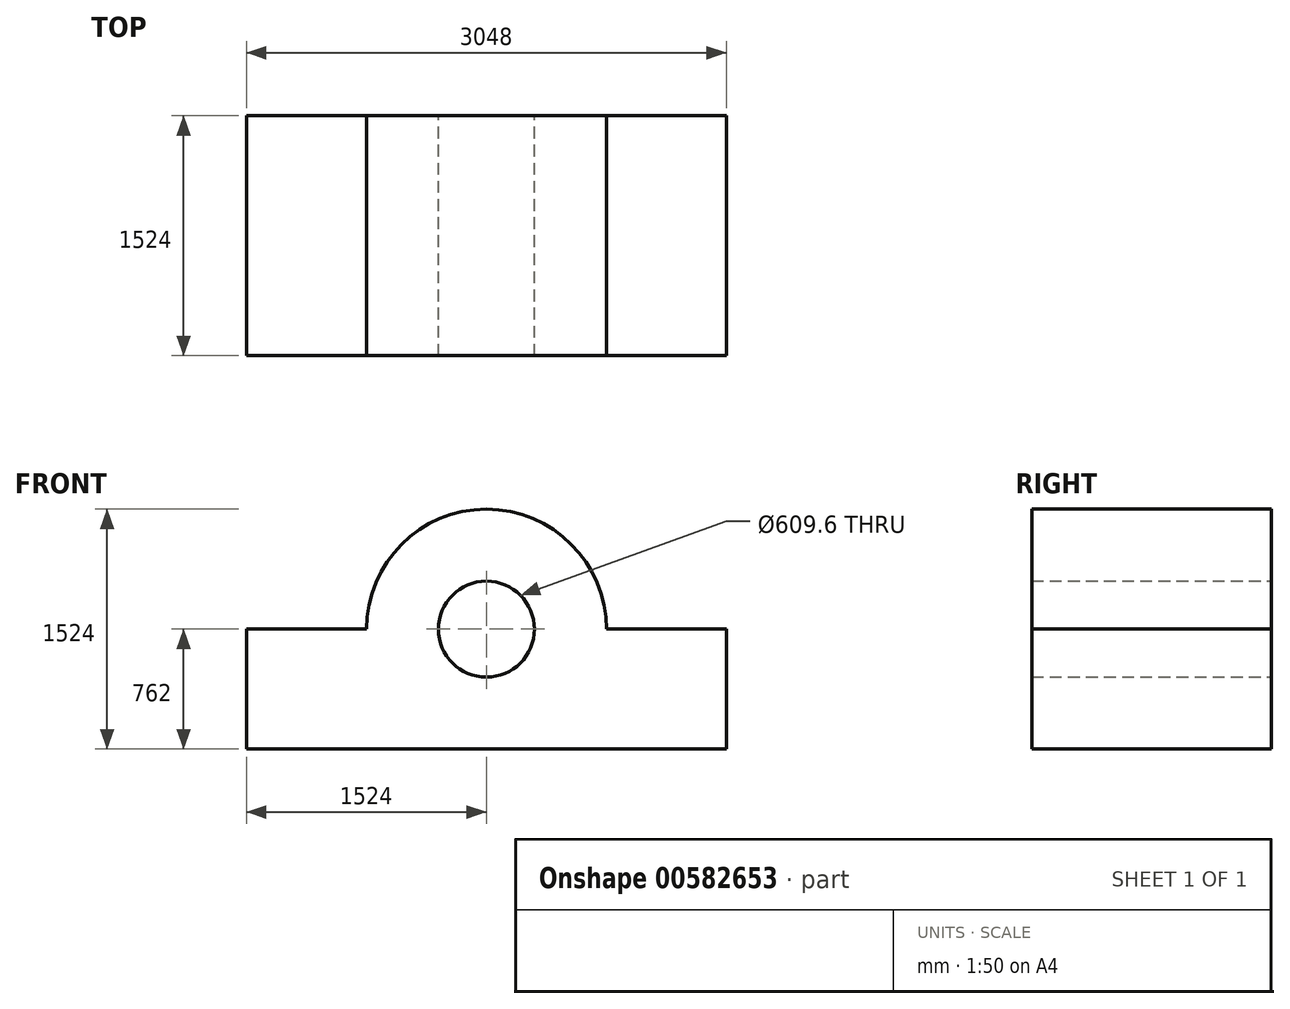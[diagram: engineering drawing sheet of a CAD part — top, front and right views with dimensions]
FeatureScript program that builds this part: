
annotation { "Feature Type Name" : "Feature", "Feature Type Description" : "" }
export const myFeature = defineFeature(function(context is Context, id is Id, definition is map)
    precondition{}
    {
        {
            var Q0;
            Q0=qCreatedBy(makeId("Front.planeOp"),FACE);
            var sketch = newSketch(context, id + "F0", { "sketchPlane" : qUnion([Q0])});
            skLineSegment(sketch, "E0", {"start": v(0, 0) * mm, "end": v(3048, 0) * mm});
            skLineSegment(sketch, "E1", {"start": v(0, 0) * mm, "end": v(0, 762) * mm});
            skLineSegment(sketch, "E2", {"start": v(3048, 0) * mm, "end": v(3048, 762) * mm});
            skLineSegment(sketch, "E3", {"start": v(0, 762) * mm, "end": v(762, 762) * mm});
            skLineSegment(sketch, "E4", {"start": v(3048, 762) * mm, "end": v(2286, 762) * mm});
            skArc(sketch, "E5", {"start": v(2286, 762) * mm, "mid": v(1524, 1524) * mm, "end": v(762, 762) * mm});
            skCircle(sketch, "E6", {"center": v(1524, 762) * mm, "radius": 304.8 * mm});
            skSolve(sketch);
        }
        {
            var Q0;
            Q0=makeQuery(id+"F0.imprint","IMPRINT",FACE,{"disambiguationData":[TD([[makeQuery(id+"F0.imprint","IMPRINT",EDGE,{"derivedFrom":sQuery(id+"F0.wireOp",EDGE,"E0")}),1.0]])]});
            extrude(context, id + "F1", {"entities" : qUnion([Q0]), "depth" : 1524 * mm, "offsetDistance" : 25.4 * mm});
        }
    });
